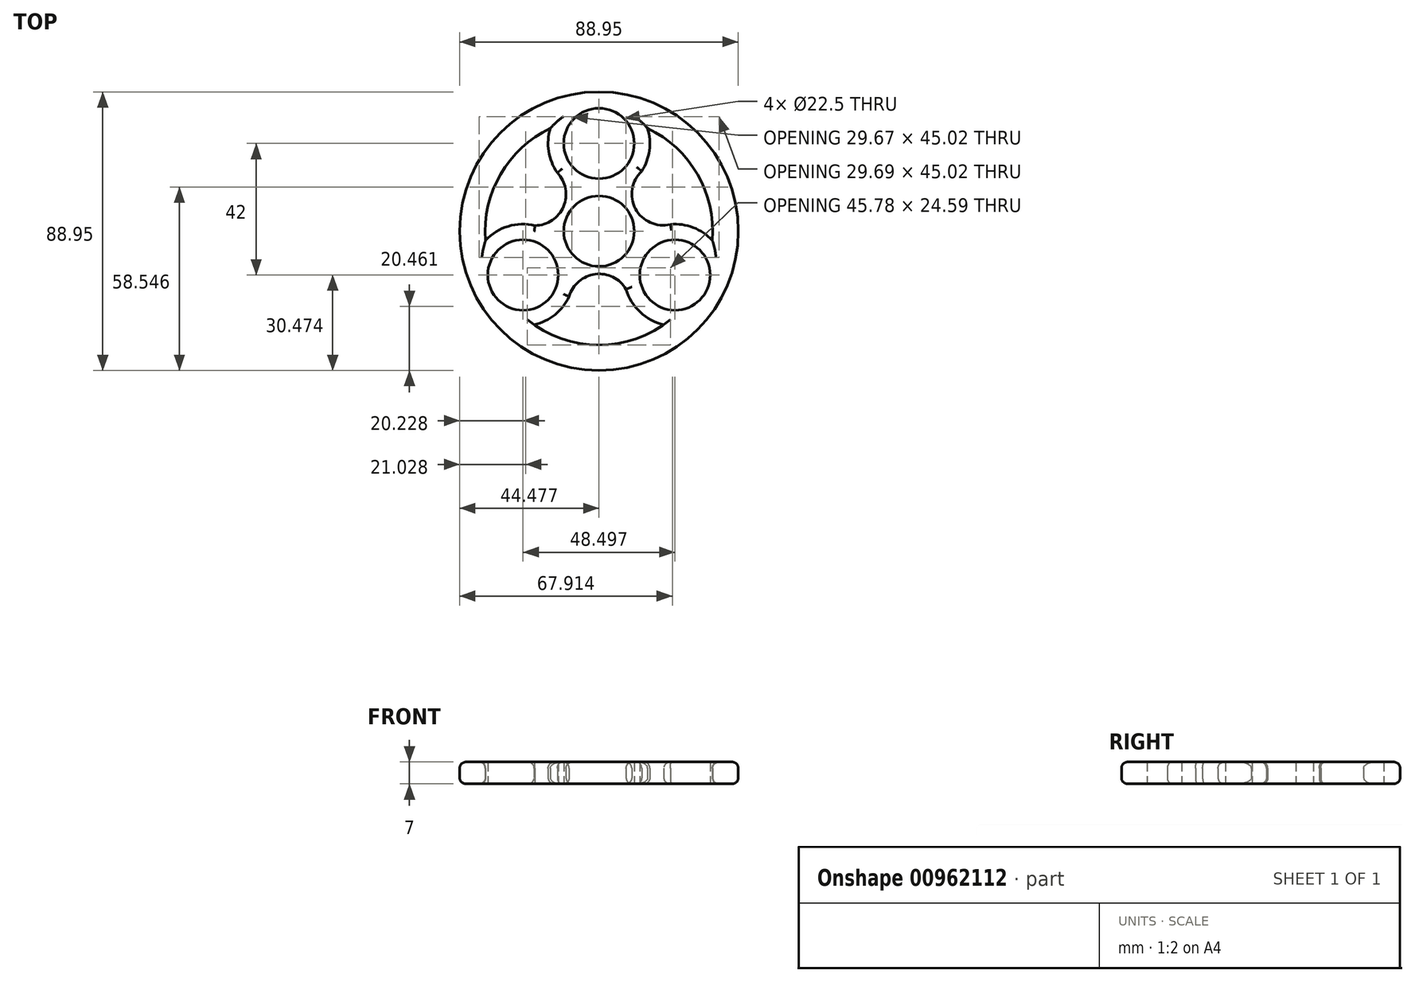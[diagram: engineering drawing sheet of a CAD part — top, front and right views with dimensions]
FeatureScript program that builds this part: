
annotation { "Feature Type Name" : "Feature", "Feature Type Description" : "" }
export const myFeature = defineFeature(function(context is Context, id is Id, definition is map)
    precondition{}
    {
        {
            var Q0;
            Q0=qCreatedBy(makeId("Top.planeOp"),FACE);
            var sketch = newSketch(context, id + "F0", { "sketchPlane" : qUnion([Q0])});
            skCircle(sketch, "E0", {"center": v(-39.25, 16.08) * mm, "radius": 11.25 * mm});
            skCircle(sketch, "E1", {"center": v(-39.25, 44.08) * mm, "radius": 11.25 * mm});
            skCircle(sketch, "E2.1.0", {"center": v(-63.5, 2.08) * mm, "radius": 11.25 * mm});
            skCircle(sketch, "E2.2.0", {"center": v(-15, 2.08) * mm, "radius": 11.25 * mm});
            skCircle(sketch, "E3.0", {"center": v(-39.25, 44.08) * mm, "radius": 16.25 * mm});
            skCircle(sketch, "E4.0", {"center": v(-63.5, 2.08) * mm, "radius": 16.25 * mm});
            skCircle(sketch, "E5.0", {"center": v(-15, 2.08) * mm, "radius": 16.25 * mm});
            skArc(sketch, "E6", {"start": v(-62.65, 18.31) * mm, "mid": v(-51.25, 22.62) * mm, "end": v(-52.55, 34.74) * mm});
            skArc(sketch, "E7.1.0", {"start": v(-29.48, -5.3) * mm, "mid": v(-38.92, 2.43) * mm, "end": v(-48.76, -4.75) * mm});
            skArc(sketch, "E7.2.0", {"start": v(-25.63, 35.23) * mm, "mid": v(-27.6, 23.2) * mm, "end": v(-16.45, 18.27) * mm});
            skCircle(sketch, "E8", {"center": v(-39.25, 16.08) * mm, "radius": 44.47 * mm});
            skCircle(sketch, "E9", {"center": v(-39.25, 16.08) * mm, "radius": 36.3 * mm});
            skSolve(sketch);
        }
        {
            var Q0;
            Q0=makeQuery(id+"F0.imprint","IMPRINT",FACE,{"disambiguationData":[TD([[makeQuery(id+"F0.imprint","IMPRINT",EDGE,{"derivedFrom":sQuery(id+"F0.wireOp",EDGE,"E1")}),-1.0]])]});
            var Q1;
            Q1=makeQuery(id+"F0.imprint","IMPRINT",FACE,{"disambiguationData":[TD([[makeQuery(id+"F0.imprint","IMPRINT",EDGE,{"derivedFrom":sQuery(id+"F0.wireOp",EDGE,"E2.1.0")}),-1.0]])]});
            var Q2;
            Q2=makeQuery(id+"F0.imprint","IMPRINT",FACE,{"disambiguationData":[TD([[makeQuery(id+"F0.imprint","IMPRINT",EDGE,{"derivedFrom":sQuery(id+"F0.wireOp",EDGE,"E2.2.0")}),-1.0]])]});
            var Q3;
            Q3=makeQuery(id+"F0.imprint","IMPRINT",FACE,{"disambiguationData":[TD([[makeQuery(id+"F0.imprint","IMPRINT",EDGE,{"derivedFrom":sQuery(id+"F0.wireOp",EDGE,"E0")}),-1.0]])]});
            var Q4;
            Q4=makeQuery(id+"F0.imprint","IMPRINT",FACE,{"disambiguationData":[TD([[makeQuery(id+"F0.imprint","IMPRINT",EDGE,{"derivedFrom":sQuery(id+"F0.wireOp",EDGE,"E8")}),1.0]])]});
            var Q5;
            {var subQ3=sQuery(id+"F0.wireOp",EDGE,"E9");var subQ10=sQuery(id+"F0.wireOp",EDGE,"E2.1.0");var subQ11=makeQuery(id+"F0.imprint","INTERSECT",VERTEX,{"disambiguationData":[OD(0.0)],"derivedFrom":[subQ10,subQ3]});Q5=makeQuery(id+"F0.imprint","IMPRINT",FACE,{"disambiguationData":[TD([[makeQuery(id+"F0.imprint","IMPRINT",EDGE,{"disambiguationData":[TD([[subQ11,1.0]])],"derivedFrom":subQ10}),-1.0]])]});}
            var Q6;
            {var subQ6=sQuery(id+"F0.wireOp",EDGE,"E9");var subQ10=sQuery(id+"F0.wireOp",EDGE,"E1");var subQ11=makeQuery(id+"F0.imprint","INTERSECT",VERTEX,{"disambiguationData":[OD(0.0)],"derivedFrom":[subQ10,subQ6]});Q6=makeQuery(id+"F0.imprint","IMPRINT",FACE,{"disambiguationData":[TD([[makeQuery(id+"F0.imprint","IMPRINT",EDGE,{"disambiguationData":[TD([[subQ11,1.0]])],"derivedFrom":subQ10}),-1.0]])]});}
            var Q7;
            {var subQ3=sQuery(id+"F0.wireOp",EDGE,"E9");var subQ10=sQuery(id+"F0.wireOp",EDGE,"E2.2.0");var subQ11=makeQuery(id+"F0.imprint","INTERSECT",VERTEX,{"disambiguationData":[OD(0.0)],"derivedFrom":[subQ10,subQ3]});Q7=makeQuery(id+"F0.imprint","IMPRINT",FACE,{"disambiguationData":[TD([[makeQuery(id+"F0.imprint","IMPRINT",EDGE,{"disambiguationData":[TD([[subQ11,1.0]])],"derivedFrom":subQ10}),-1.0]])]});}
            var Q8;
            {var subQ0=sQuery(id+"F0.wireOp",EDGE,"E5.0");var subQ2=sQuery(id+"F0.wireOp",EDGE,"cf1ca84c-4af9-40a5-9260-191c833b9b89.2.3.0");var subQ9=makeQuery(id+"F0.imprint","INTERSECT",VERTEX,{"disambiguationData":[OD(0.0)],"derivedFrom":[subQ0,subQ2]});Q8=makeQuery(id+"F0.imprint","IMPRINT",FACE,{"disambiguationData":[TD([[makeQuery(id+"F0.imprint","IMPRINT",EDGE,{"disambiguationData":[TD([[subQ9,-1.0]])],"derivedFrom":subQ0}),1.0]])]});}
            var Q9;
            {var subQ4=sQuery(id+"F0.wireOp",EDGE,"QsNSEYDM-KLoN-78Qe-ZYG4-Gf3tMeu0RkRC");var subQ7=sQuery(id+"F0.wireOp",EDGE,"E7.2.0");var subQ8=makeQuery(id+"F0.imprint","INTERSECT",VERTEX,{"disambiguationData":[OD(0.0)],"derivedFrom":[subQ7,subQ4]});Q9=makeQuery(id+"F0.imprint","IMPRINT",FACE,{"disambiguationData":[TD([[makeQuery(id+"F0.imprint","IMPRINT",EDGE,{"disambiguationData":[TD([[subQ8,-1.0]])],"derivedFrom":subQ7}),-1.0]])]});}
            var Q10;
            {var subQ0=sQuery(id+"F0.wireOp",EDGE,"QsNSEYDM-KLoN-78Qe-ZYG4-Gf3tMeu0RkRC");var subQ1=sQuery(id+"F0.wireOp",EDGE,"E9");var subQ2=makeQuery(id+"F0.imprint","INTERSECT",VERTEX,{"disambiguationData":[OD(0.0)],"derivedFrom":[subQ1,subQ0]});Q10=makeQuery(id+"F0.imprint","IMPRINT",FACE,{"disambiguationData":[TD([[makeQuery(id+"F0.imprint","IMPRINT",EDGE,{"disambiguationData":[TD([[subQ2,-1.0]])],"derivedFrom":subQ1}),-1.0]])]});}
            var Q11;
            {var subQ0=sQuery(id+"F0.wireOp",EDGE,"E9");var subQ1=sQuery(id+"F0.wireOp",EDGE,"E5.0");var subQ2=makeQuery(id+"F0.imprint","INTERSECT",VERTEX,{"disambiguationData":[OD(0.0)],"derivedFrom":[subQ1,subQ0]});Q11=makeQuery(id+"F0.imprint","IMPRINT",FACE,{"disambiguationData":[TD([[makeQuery(id+"F0.imprint","IMPRINT",EDGE,{"disambiguationData":[TD([[subQ2,-1.0]])],"derivedFrom":subQ1}),1.0]])]});}
            var Q12;
            {var subQ0=sQuery(id+"F0.wireOp",EDGE,"cf1ca84c-4af9-40a5-9260-191c833b9b89.2.3.0");var subQ1=sQuery(id+"F0.wireOp",EDGE,"E5.0");var subQ2=makeQuery(id+"F0.imprint","INTERSECT",VERTEX,{"disambiguationData":[OD(0.0)],"derivedFrom":[subQ1,subQ0]});Q12=makeQuery(id+"F0.imprint","IMPRINT",FACE,{"disambiguationData":[TD([[makeQuery(id+"F0.imprint","IMPRINT",EDGE,{"disambiguationData":[TD([[subQ2,1.0]])],"derivedFrom":subQ1}),1.0]])]});}
            var Q13;
            {var subQ0=sQuery(id+"F0.wireOp",EDGE,"cf1ca84c-4af9-40a5-9260-191c833b9b89.2.4.0");var subQ1=sQuery(id+"F0.wireOp",EDGE,"E3.0");var subQ2=makeQuery(id+"F0.imprint","INTERSECT",VERTEX,{"disambiguationData":[OD(0.0)],"derivedFrom":[subQ1,subQ0]});Q13=makeQuery(id+"F0.imprint","IMPRINT",FACE,{"disambiguationData":[TD([[makeQuery(id+"F0.imprint","IMPRINT",EDGE,{"disambiguationData":[TD([[subQ2,1.0]])],"derivedFrom":subQ1}),1.0]])]});}
            var Q14;
            {var subQ0=sQuery(id+"F0.wireOp",EDGE,"E6");var subQ1=sQuery(id+"F0.wireOp",EDGE,"E4.0");var subQ2=makeQuery(id+"F0.imprint","INTERSECT",VERTEX,{"disambiguationData":[OD(0.0)],"derivedFrom":[subQ1,subQ0]});Q14=makeQuery(id+"F0.imprint","IMPRINT",FACE,{"disambiguationData":[TD([[makeQuery(id+"F0.imprint","IMPRINT",EDGE,{"disambiguationData":[TD([[subQ2,1.0]])],"derivedFrom":subQ1}),1.0]])]});}
            var Q15;
            {var subQ0=sQuery(id+"F0.wireOp",EDGE,"E5.0");var subQ1=sQuery(id+"F0.wireOp",EDGE,"E7.1.0");var subQ2=makeQuery(id+"F0.imprint","INTERSECT",VERTEX,{"disambiguationData":[OD(0.0)],"derivedFrom":[subQ1,subQ0]});Q15=makeQuery(id+"F0.imprint","IMPRINT",FACE,{"disambiguationData":[TD([[makeQuery(id+"F0.imprint","IMPRINT",EDGE,{"disambiguationData":[TD([[subQ2,-1.0]])],"derivedFrom":subQ1}),1.0]])]});}
            var Q16;
            {var subQ0=sQuery(id+"F0.wireOp",EDGE,"QsNSEYDM-KLoN-78Qe-ZYG4-Gf3tMeu0RkRC");var subQ1=sQuery(id+"F0.wireOp",EDGE,"E7.2.0");var subQ2=makeQuery(id+"F0.imprint","INTERSECT",VERTEX,{"disambiguationData":[OD(0.0)],"derivedFrom":[subQ1,subQ0]});Q16=makeQuery(id+"F0.imprint","IMPRINT",FACE,{"disambiguationData":[TD([[makeQuery(id+"F0.imprint","IMPRINT",EDGE,{"disambiguationData":[TD([[subQ2,-1.0]])],"derivedFrom":subQ1}),1.0]])]});}
            extrude(context, id + "F1", {"entities" : qUnion([Q0, Q1, Q2, Q3, Q4, Q5, Q6, Q7, Q8, Q9, Q10, Q11, Q12, Q13, Q14, Q15, Q16]), "depth" : 7 * mm, "offsetDistance" : 25 * mm});
        }
        {
            var Q0;
            Q0=makeQuery(id+"F1.opExtrude","CAP_EDGE",EDGE,{"disambiguationData":[OSD([sQuery(id+"F0.wireOp",EDGE,"E5.0")])],"isStart":false});
            var Q1;
            Q1=makeQuery(id+"F1.opExtrude","CAP_EDGE",EDGE,{"disambiguationData":[OSD([sQuery(id+"F0.wireOp",EDGE,"E7.2.0")])],"isStart":false});
            var Q2;
            Q2=makeQuery(id+"F1.opExtrude","CAP_EDGE",EDGE,{"disambiguationData":[OSD([sQuery(id+"F0.wireOp",EDGE,"E7.1.0")])],"isStart":false});
            var Q3;
            Q3=makeQuery(id+"F1.opExtrude","CAP_EDGE",EDGE,{"disambiguationData":[OSD([sQuery(id+"F0.wireOp",EDGE,"E4.0")])],"isStart":false});
            var Q4;
            Q4=makeQuery(id+"F1.opExtrude","CAP_EDGE",EDGE,{"disambiguationData":[OSD([sQuery(id+"F0.wireOp",EDGE,"E6")])],"isStart":false});
            var Q5;
            Q5=makeQuery(id+"F1.opExtrude","CAP_EDGE",EDGE,{"disambiguationData":[OSD([sQuery(id+"F0.wireOp",EDGE,"E3.0")])],"isStart":false});
            var Q6;
            Q6=makeQuery(id+"F1.opExtrude","CAP_EDGE",EDGE,{"disambiguationData":[OSD([sQuery(id+"F0.wireOp",EDGE,"E4.0")])],"isStart":true});
            var Q7;
            Q7=makeQuery(id+"F1.opExtrude","CAP_EDGE",EDGE,{"disambiguationData":[OSD([sQuery(id+"F0.wireOp",EDGE,"E7.1.0")])],"isStart":true});
            var Q8;
            Q8=makeQuery(id+"F1.opExtrude","CAP_EDGE",EDGE,{"disambiguationData":[OSD([sQuery(id+"F0.wireOp",EDGE,"E6")])],"isStart":true});
            var Q9;
            Q9=makeQuery(id+"F1.opExtrude","CAP_EDGE",EDGE,{"disambiguationData":[OSD([sQuery(id+"F0.wireOp",EDGE,"E5.0")])],"isStart":true});
            var Q10;
            Q10=makeQuery(id+"F1.opExtrude","CAP_EDGE",EDGE,{"disambiguationData":[OSD([sQuery(id+"F0.wireOp",EDGE,"E7.2.0")])],"isStart":true});
            var Q11;
            Q11=makeQuery(id+"F1.opExtrude","CAP_EDGE",EDGE,{"disambiguationData":[OSD([sQuery(id+"F0.wireOp",EDGE,"E3.0")])],"isStart":true});
            var Q12;
            {var subQ0=sQuery(id+"F0.wireOp",EDGE,"E9");Q12=makeQuery(id+"F1.opExtrude","CAP_EDGE",EDGE,{"disambiguationData":[OSD([subQ0]),TDD([makeQuery(id+"F0.imprint","IMPRINT",EDGE,{"disambiguationData":[TD([[makeQuery(id+"F0.imprint","INTERSECT",VERTEX,{"disambiguationData":[OD(0.0)],"derivedFrom":[sQuery(id+"F0.wireOp",EDGE,"E3.0"),subQ0]}),-1.0]])],"derivedFrom":subQ0})])],"isStart":false});}
            var Q13;
            Q13=makeQuery(id+"F1.opExtrude","CAP_EDGE",EDGE,{"disambiguationData":[OSD([sQuery(id+"F0.wireOp",EDGE,"E8")])],"isStart":false});
            var Q14;
            {var subQ0=sQuery(id+"F0.wireOp",EDGE,"E9");Q14=makeQuery(id+"F1.opExtrude","CAP_EDGE",EDGE,{"disambiguationData":[OSD([subQ0]),TDD([makeQuery(id+"F0.imprint","IMPRINT",EDGE,{"disambiguationData":[TD([[makeQuery(id+"F0.imprint","INTERSECT",VERTEX,{"disambiguationData":[OD(0.0)],"derivedFrom":[sQuery(id+"F0.wireOp",EDGE,"E4.0"),subQ0]}),-1.0]])],"derivedFrom":subQ0})])],"isStart":false});}
            var Q15;
            {var subQ0=sQuery(id+"F0.wireOp",EDGE,"E9");Q15=makeQuery(id+"F1.opExtrude","CAP_EDGE",EDGE,{"disambiguationData":[OSD([subQ0]),TDD([makeQuery(id+"F0.imprint","IMPRINT",EDGE,{"disambiguationData":[TD([[makeQuery(id+"F0.imprint","INTERSECT",VERTEX,{"disambiguationData":[OD(1.0)],"derivedFrom":[sQuery(id+"F0.wireOp",EDGE,"E3.0"),subQ0]}),1.0]])],"derivedFrom":subQ0})])],"isStart":true});}
            var Q16;
            Q16=makeQuery(id+"F1.opExtrude","CAP_EDGE",EDGE,{"disambiguationData":[OSD([sQuery(id+"F0.wireOp",EDGE,"E8")])],"isStart":true});
            var Q17;
            {var subQ0=sQuery(id+"F0.wireOp",EDGE,"E9");Q17=makeQuery(id+"F1.opExtrude","CAP_EDGE",EDGE,{"disambiguationData":[OSD([subQ0]),TDD([makeQuery(id+"F0.imprint","IMPRINT",EDGE,{"disambiguationData":[TD([[makeQuery(id+"F0.imprint","INTERSECT",VERTEX,{"disambiguationData":[OD(0.0)],"derivedFrom":[sQuery(id+"F0.wireOp",EDGE,"E3.0"),subQ0]}),-1.0]])],"derivedFrom":subQ0})])],"isStart":true});}
            var Q18;
            {var subQ0=sQuery(id+"F0.wireOp",EDGE,"E9");Q18=makeQuery(id+"F1.opExtrude","CAP_EDGE",EDGE,{"disambiguationData":[OSD([subQ0]),TDD([makeQuery(id+"F0.imprint","IMPRINT",EDGE,{"disambiguationData":[TD([[makeQuery(id+"F0.imprint","INTERSECT",VERTEX,{"disambiguationData":[OD(0.0)],"derivedFrom":[sQuery(id+"F0.wireOp",EDGE,"E4.0"),subQ0]}),-1.0]])],"derivedFrom":subQ0})])],"isStart":true});}
            var Q19;
            {var subQ0=sQuery(id+"F0.wireOp",EDGE,"E9");Q19=makeQuery(id+"F1.opExtrude","CAP_EDGE",EDGE,{"disambiguationData":[OSD([subQ0]),TDD([makeQuery(id+"F0.imprint","IMPRINT",EDGE,{"disambiguationData":[TD([[makeQuery(id+"F0.imprint","INTERSECT",VERTEX,{"disambiguationData":[OD(1.0)],"derivedFrom":[sQuery(id+"F0.wireOp",EDGE,"E3.0"),subQ0]}),1.0]])],"derivedFrom":subQ0})])],"isStart":false});}
            var Q20;
            {var subQ0=sQuery(id+"F0.wireOp",EDGE,"E5.0");Q20=makeQuery(id+"F1.opExtrude","CAP_EDGE",EDGE,{"disambiguationData":[OSD([subQ0]),TDD([makeQuery(id+"F0.imprint","IMPRINT",EDGE,{"disambiguationData":[TD([[makeQuery(id+"F0.imprint","INTERSECT",VERTEX,{"derivedFrom":[sQuery(id+"F0.wireOp",EDGE,"E7.2.0"),subQ0]}),1.0]])],"derivedFrom":subQ0})])],"isStart":true});}
            var Q21;
            {var subQ0=sQuery(id+"F0.wireOp",EDGE,"QsNSEYDM-KLoN-78Qe-ZYG4-Gf3tMeu0RkRC");var subQ1=sQuery(id+"F0.wireOp",EDGE,"E7.2.0");var subQ2=makeQuery(id+"F0.imprint","INTERSECT",VERTEX,{"disambiguationData":[OD(0.0)],"derivedFrom":[subQ1,subQ0]});Q21=makeQuery(id+"F1.opExtrude","CAP_EDGE",EDGE,{"disambiguationData":[OSD([subQ0]),TDD([makeQuery(id+"F0.imprint","IMPRINT",EDGE,{"disambiguationData":[TD([[subQ2,1.0]])],"derivedFrom":subQ0}),makeQuery(id+"F0.imprint","IMPRINT",EDGE,{"disambiguationData":[TD([[subQ2,-1.0]])],"derivedFrom":subQ0})])],"isStart":false});}
            var Q22;
            {var subQ0=sQuery(id+"F0.wireOp",EDGE,"QsNSEYDM-KLoN-78Qe-ZYG4-Gf3tMeu0RkRC");Q22=makeQuery(id+"F1.opExtrude","CAP_EDGE",EDGE,{"disambiguationData":[OSD([subQ0]),TDD([makeQuery(id+"F0.imprint","IMPRINT",EDGE,{"disambiguationData":[TD([[makeQuery(id+"F0.imprint","INTERSECT",VERTEX,{"derivedFrom":[sQuery(id+"F0.wireOp",EDGE,"cf1ca84c-4af9-40a5-9260-191c833b9b89.2.3.0"),subQ0]}),1.0]])],"derivedFrom":subQ0})])],"isStart":false});}
            var Q23;
            {var subQ0=sQuery(id+"F0.wireOp",EDGE,"E5.0");var subQ1=sQuery(id+"F0.wireOp",EDGE,"E7.1.0");var subQ2=makeQuery(id+"F0.imprint","INTERSECT",VERTEX,{"disambiguationData":[OD(0.0)],"derivedFrom":[subQ1,subQ0]});Q23=makeQuery(id+"F1.opExtrude","CAP_EDGE",EDGE,{"disambiguationData":[OSD([subQ0]),TDD([makeQuery(id+"F0.imprint","IMPRINT",EDGE,{"disambiguationData":[TD([[subQ2,1.0]])],"derivedFrom":subQ0}),makeQuery(id+"F0.imprint","IMPRINT",EDGE,{"disambiguationData":[TD([[subQ2,-1.0]])],"derivedFrom":subQ0})])],"isStart":false});}
            var Q24;
            {var subQ0=sQuery(id+"F0.wireOp",EDGE,"QsNSEYDM-KLoN-78Qe-ZYG4-Gf3tMeu0RkRC");Q24=makeQuery(id+"F1.opExtrude","CAP_EDGE",EDGE,{"disambiguationData":[OSD([subQ0]),TDD([makeQuery(id+"F0.imprint","IMPRINT",EDGE,{"disambiguationData":[TD([[makeQuery(id+"F0.imprint","INTERSECT",VERTEX,{"derivedFrom":[sQuery(id+"F0.wireOp",EDGE,"cf1ca84c-4af9-40a5-9260-191c833b9b89.2.3.0"),subQ0]}),1.0]])],"derivedFrom":subQ0})])],"isStart":true});}
            var Q25;
            {var subQ0=sQuery(id+"F0.wireOp",EDGE,"E5.0");var subQ1=sQuery(id+"F0.wireOp",EDGE,"E7.1.0");var subQ2=makeQuery(id+"F0.imprint","INTERSECT",VERTEX,{"disambiguationData":[OD(0.0)],"derivedFrom":[subQ1,subQ0]});Q25=makeQuery(id+"F1.opExtrude","CAP_EDGE",EDGE,{"disambiguationData":[OSD([subQ0]),TDD([makeQuery(id+"F0.imprint","IMPRINT",EDGE,{"disambiguationData":[TD([[subQ2,1.0]])],"derivedFrom":subQ0}),makeQuery(id+"F0.imprint","IMPRINT",EDGE,{"disambiguationData":[TD([[subQ2,-1.0]])],"derivedFrom":subQ0})])],"isStart":true});}
            var Q26;
            {var subQ0=sQuery(id+"F0.wireOp",EDGE,"QsNSEYDM-KLoN-78Qe-ZYG4-Gf3tMeu0RkRC");var subQ1=sQuery(id+"F0.wireOp",EDGE,"E7.2.0");var subQ2=makeQuery(id+"F0.imprint","INTERSECT",VERTEX,{"disambiguationData":[OD(0.0)],"derivedFrom":[subQ1,subQ0]});Q26=makeQuery(id+"F1.opExtrude","CAP_EDGE",EDGE,{"disambiguationData":[OSD([subQ0]),TDD([makeQuery(id+"F0.imprint","IMPRINT",EDGE,{"disambiguationData":[TD([[subQ2,1.0]])],"derivedFrom":subQ0}),makeQuery(id+"F0.imprint","IMPRINT",EDGE,{"disambiguationData":[TD([[subQ2,-1.0]])],"derivedFrom":subQ0})])],"isStart":true});}
            var Q27;
            {var subQ0=sQuery(id+"F0.wireOp",EDGE,"E5.0");Q27=makeQuery(id+"F1.opExtrude","CAP_EDGE",EDGE,{"disambiguationData":[OSD([subQ0]),TDD([makeQuery(id+"F0.imprint","IMPRINT",EDGE,{"disambiguationData":[TD([[makeQuery(id+"F0.imprint","INTERSECT",VERTEX,{"derivedFrom":[sQuery(id+"F0.wireOp",EDGE,"E7.2.0"),subQ0]}),1.0]])],"derivedFrom":subQ0})])],"isStart":false});}
            fillet(context, id + "F2", {"entities" : qUnion([Q0, Q1, Q2, Q3, Q4, Q5, Q6, Q7, Q8, Q9, Q10, Q11, Q12, Q13, Q14, Q15, Q16, Q17, Q18, Q19, Q20, Q21, Q22, Q23, Q24, Q25, Q26, Q27]), "radius" : 2 * mm, "tangentPropagation" : true, "allowEdgeOverflow" : false});
        }
    });
